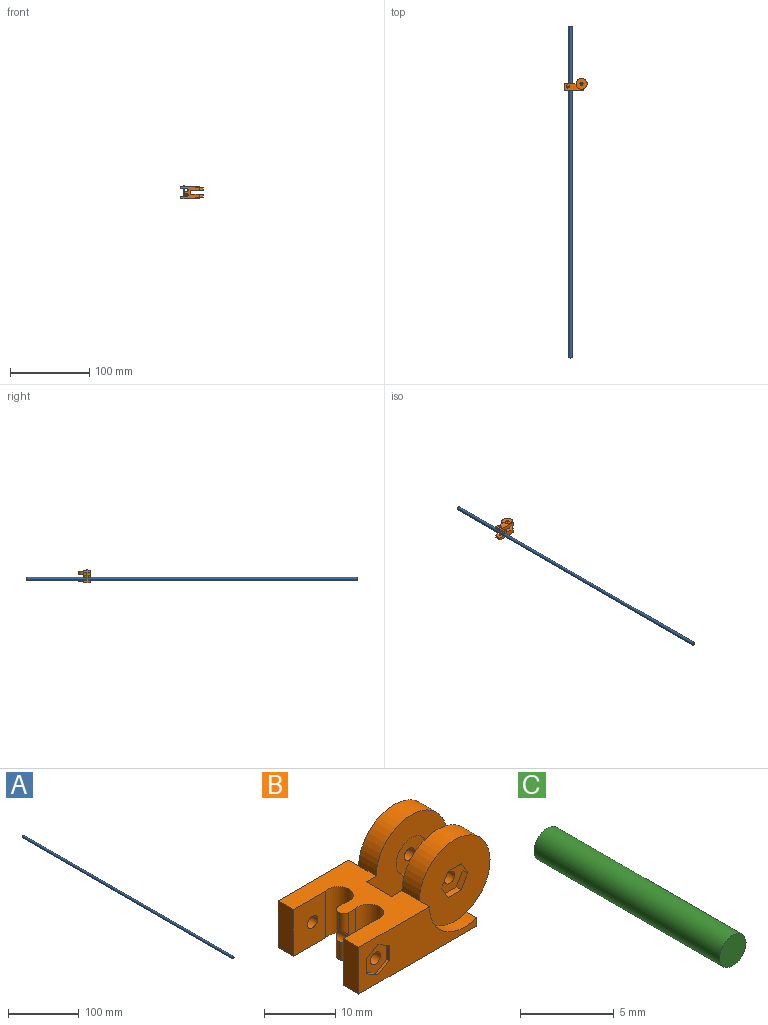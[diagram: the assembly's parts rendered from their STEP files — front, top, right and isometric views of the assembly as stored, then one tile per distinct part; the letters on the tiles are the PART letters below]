
ASSEMBLY  parts=3 mates=2
PART A: 4 faces, bbox 4x420x4 mm
  f0: cylinder r=1mm len=420mm, axis (0,1,0), area 2638.9mm2, adj f2,f3
  f1: cylinder r=2mm len=420mm, axis (0,1,0), area 5277.9mm2, adj f2,f3
  f2: plane 4x4mm, normal (0,-1,0), area 9.4mm2, adj f0,f1
  f3: plane 4x4mm, normal (0,1,0), area 9.4mm2, adj f0,f1
PART B: 54 faces, bbox 28x16x15 mm
  f0: cylinder r=1mm len=2.55mm, axis (0,-1,0), area 16mm2, adj f37,f51
  f1: plane 23.36x8mm, normal (0,-1,0), area 114.7mm2, adj f4,f5,f9,f10,f17,f43,f44,f45
  f2: cylinder r=1mm len=2.55mm, axis (0,-1,0), area 16mm2, adj f38,f49
  f3: plane 3.02x0.1mm, normal (-1,0,0), area 0.3mm2, adj f9,f42,f52,f53
  f4: plane 8x3.05mm, normal (-1,0,0), area 24.4mm2, adj f1,f5,f9,f38
  f5: plane 16x14mm, normal (0,0,1), area 137mm2, adj f1,f4,f11,f12,f14,f15,f17,f18
  f6: cylinder r=1mm len=2mm, axis (0,-1,0), area 12.6mm2, adj f21,f34
  f7: plane 14x14mm, normal (0,-1,0), area 136.4mm2, adj f11,f17,f26,f27,f28,f29,f30,f31
  f8: cylinder r=1mm len=2mm, axis (0,-1,0), area 12.6mm2, adj f22,f32
  f9: plane 23.36x16mm, normal (0,0,-1), area 239mm2, adj f1,f3,f4,f10,f15,f16,f18,f23
  f10: plane 5.45x1.41mm, normal (1,0,0), area 7.7mm2, adj f1,f9,f11,f17,f24
  f11: cylinder r=7mm len=14mm, axis (0,1,0), area 105.5mm2, adj f5,f7,f10,f24
  f12: cylinder r=7mm len=14mm, axis (0,1,0), area 105.5mm2, adj f5,f16,f19,f25
  f13: cylinder r=3.05mm len=6.1mm, axis (0,-1,0), area 8.6mm2, adj f22,f24
  f14: cylinder r=7mm len=9.36mm, axis (0,1,0), area 26.8mm2, adj f5,f16,f18,f19
  f15: plane 8x3.05mm, normal (-1,0,0), area 24.4mm2, adj f5,f9,f18,f37
  f16: plane 5.45x1.41mm, normal (1,0,0), area 7.7mm2, adj f9,f12,f14,f18,f25
  f17: cylinder r=7mm len=9.36mm, axis (0,1,0), area 26.8mm2, adj f1,f5,f7,f10
  f18: plane 23.36x8mm, normal (0,1,0), area 116.3mm2, adj f5,f9,f14,f15,f16,f50
  f19: plane 14x14mm, normal (0,1,0), area 138mm2, adj f12,f14,f33
  f20: cylinder r=3.05mm len=6.1mm, axis (0,-1,0), area 8.6mm2, adj f21,f25
  f21: plane 6.1x6.1mm, normal (0,-1,0), area 26.1mm2, adj f6,f20
  f22: plane 6.1x6.1mm, normal (0,1,0), area 26.1mm2, adj f8,f13
  f23: plane 8x5.1mm, normal (1,0,0), area 40.8mm2, adj f5,f9,f24,f25
  f24: plane 16x15mm, normal (0,1,0), area 160.9mm2, adj f5,f9,f10,f11,f13,f23
  f25: plane 16x15mm, normal (0,-1,0), area 160.9mm2, adj f5,f9,f12,f16,f20,f23
  f26: plane 2.6x1mm, normal (0,0,-1), area 2.6mm2, adj f7,f27,f31,f32
  f27: plane 2.25x1.3mm, normal (0.87,0,-0.5), area 2.6mm2, adj f7,f26,f28,f32
  f28: plane 2.25x1.3mm, normal (0.87,0,0.5), area 2.6mm2, adj f7,f27,f29,f32
  f29: plane 2.6x1mm, normal (0,0,1), area 2.6mm2, adj f7,f28,f30,f32
  f30: plane 2.25x1.3mm, normal (-0.87,0,0.5), area 2.6mm2, adj f7,f29,f31,f32
  f31: plane 2.25x1.3mm, normal (-0.87,0,-0.5), area 2.6mm2, adj f7,f26,f30,f32
  f32: plane 5.2x4.5mm, normal (0,-1,0), area 14.4mm2, adj f8,f26,f27,f28,f29,f30,f31
  f33: cylinder r=2.25mm len=4.5mm, axis (0,1,0), area 14.1mm2, adj f19,f34
  f34: plane 4.5x4.5mm, normal (0,1,0), area 12.8mm2, adj f6,f33
  f35: plane 8x1.37mm, normal (0,1,0), area 10.9mm2, adj f5,f9,f36,f53
  f36: cylinder r=2.05mm len=8mm, axis (0,0,1), area 61.8mm2, adj f5,f9,f35,f37
  f37: plane 8x6.37mm, normal (0,-1,0), area 47.8mm2, adj f0,f5,f9,f15,f36
  f38: plane 8x6.37mm, normal (0,1,0), area 47.8mm2, adj f2,f4,f5,f9,f39
  f39: cylinder r=2.05mm len=8mm, axis (0,0,1), area 61.8mm2, adj f5,f9,f38,f40
  f40: plane 8x1.37mm, normal (0,-1,0), area 10.9mm2, adj f5,f9,f39,f52
  f41: plane 3.02x0.1mm, normal (-1,0,0), area 0.3mm2, adj f5,f42,f52,f53
  f42: cylinder r=1mm len=2.06mm, axis (0,-1,0), area 4.7mm2, adj f3,f41,f52,f53
  f43: plane 2.6x0.5mm, normal (-1,0,0), area 1.3mm2, adj f1,f44,f48,f49
  f44: plane 2.25x1.3mm, normal (-0.5,0,-0.87), area 1.3mm2, adj f1,f43,f45,f49
  f45: plane 2.25x1.3mm, normal (0.5,0,-0.87), area 1.3mm2, adj f1,f44,f46,f49
  f46: plane 2.6x0.5mm, normal (1,0,0), area 1.3mm2, adj f1,f45,f47,f49
  f47: plane 2.25x1.3mm, normal (0.5,0,0.87), area 1.3mm2, adj f1,f46,f48,f49
  f48: plane 2.25x1.3mm, normal (-0.5,0,0.87), area 1.3mm2, adj f1,f43,f47,f49
  f49: plane 5.2x4.5mm, normal (0,-1,0), area 14.4mm2, adj f2,f43,f44,f45,f46,f47,f48
  f50: cylinder r=2.25mm len=4.5mm, axis (0,1,0), area 7.1mm2, adj f18,f51
  f51: plane 4.5x4.5mm, normal (0,1,0), area 12.8mm2, adj f0,f50
  f52: cylinder r=1mm len=8mm, axis (0,0,-1), area 10.3mm2, adj f3,f5,f9,f40,f41,f42
  f53: cylinder r=1mm len=8mm, axis (0,0,1), area 10.3mm2, adj f3,f5,f9,f35,f41,f42
PART C: 3 faces, bbox 2x14x2 mm
  f0: cylinder r=1mm len=14mm, axis (0,1,0), area 88mm2, adj f1,f2
  f1: plane 2x2mm, normal (0,-1,0), area 3.1mm2, adj f0
  f2: plane 2x2mm, normal (0,1,0), area 3.1mm2, adj f0
PLACE A t=(5.53,100.1,-4.65)mm fixed
PLACE B rot(axis=(-1,0,0),90deg) t=(10.53,22.98,-1.65)mm
PLACE C rot(axis=(1,0,0),90deg) t=(2.33,22.98,7.4)mm
MATE slider A.f1 <-> B.f36  axis (0,1,0) through (5.53,100.1,-4.65)mm
MATE fastened B.f0 <-> C.f0  axis (0,0,1) through (2.33,22.98,-6.6)mm
